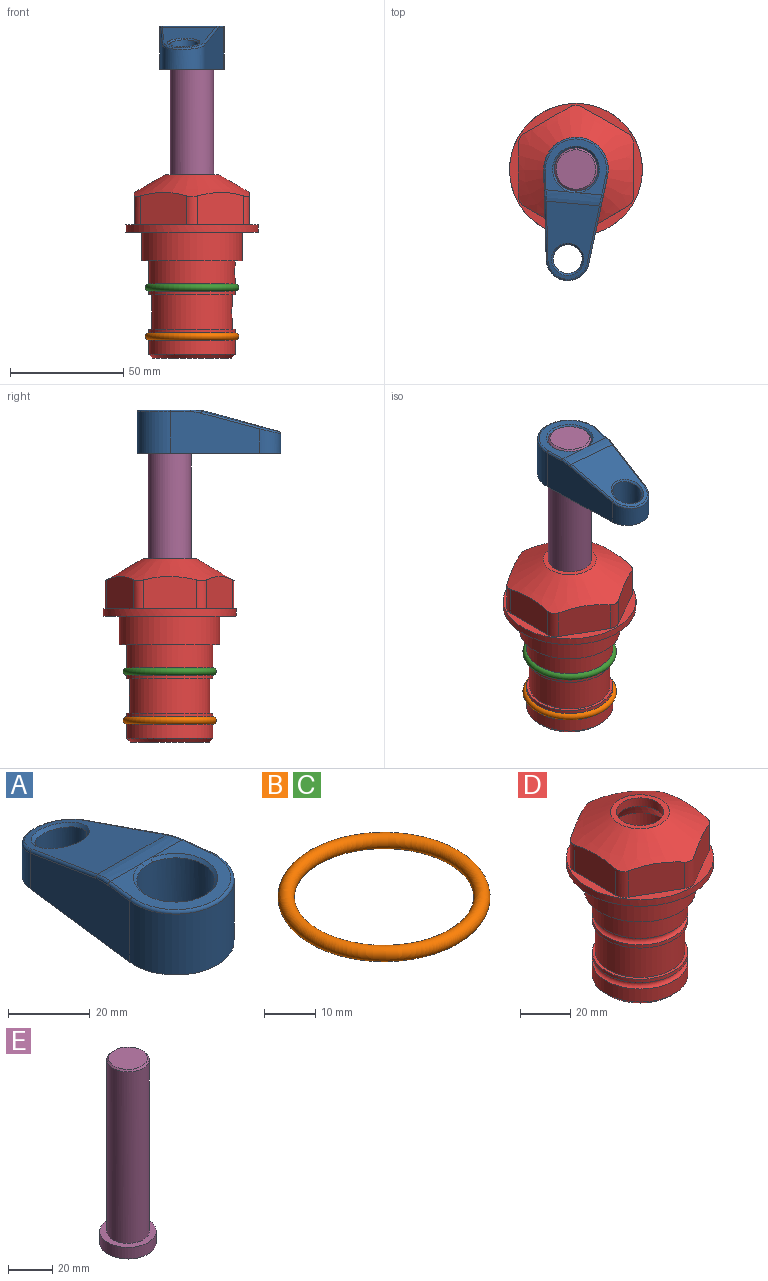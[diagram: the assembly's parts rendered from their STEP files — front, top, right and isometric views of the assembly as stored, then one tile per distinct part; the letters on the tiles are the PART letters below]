
ASSEMBLY  parts=5 mates=4
PART A: 31 faces, bbox 31.7x65.5x19.8 mm
  f0: plane 39.12x18.26mm, normal (0.99,0.12,0), area 612.2mm2, adj f1,f4,f7,f11,f13,f15
  f1: cylinder r=9.53mm len=18.91mm, axis (0,0,-1), area 296.1mm2, adj f0,f2,f7,f17
  f2: plane 39.12x18.26mm, normal (-0.99,0.12,0), area 612.2mm2, adj f1,f4,f7,f12,f14,f16
  f3: cylinder r=6.35mm len=12.7mm, axis (0,0,-1), area 362.4mm2, adj f7,f18
  f4: cylinder r=14.29mm len=28.58mm, axis (0,0,-1), area 882.2mm2, adj f0,f2,f7,f10
  f5: cylinder r=9.53mm len=19.05mm, axis (0,0,-1), area 1092.6mm2, adj f7,f19,f20
  f6: plane 26.99x23.69mm, normal (0,0,1), area 216.2mm2, adj f9,f10,f11,f12,f19
  f7: plane 63.5x28.58mm, normal (0,0,-1), area 661.8mm2, adj f0,f1,f2,f3,f4,f5,f22,f23
  f8: plane 33.52x23.6mm, normal (0,0.26,0.97), area 486mm2, adj f9,f15,f16,f17,f18
  f9: cylinder r=19.05mm len=24.72mm, axis (1,0,0), area 120.4mm2, adj f6,f8,f13,f14,f20
  f10: torus R=13.49mm, axis (0,0,1), area 59mm2, adj f4,f6,f11,f12
  f11: cylinder r=0.79mm len=8.67mm, axis (0.12,-0.99,0), area 10.8mm2, adj f0,f6,f10,f13
  f12: cylinder r=0.79mm len=8.67mm, axis (0.12,0.99,0), area 10.8mm2, adj f2,f6,f10,f14
  f13: bspline ~4.95x1.42mm, area 6.1mm2, adj f0,f9,f11,f15
  f14: bspline ~4.95x1.42mm, area 6.1mm2, adj f2,f9,f12,f16
  f15: cylinder r=0.79mm len=25.95mm, axis (0.12,-0.96,0.26), area 32.9mm2, adj f0,f8,f13,f17
  f16: cylinder r=0.79mm len=25.95mm, axis (0.12,0.96,-0.26), area 32.9mm2, adj f2,f8,f14,f17
  f17: bspline ~18.91x8.38mm, area 30mm2, adj f1,f8,f15,f16
  f18: bspline ~14.29x14.29mm, area 48.3mm2, adj f3,f8
  f19: cone r=9.53mm half-angle=45deg, axis (0,0,1), area 66.5mm2, adj f5,f6,f20
  f20: bspline ~3.22x0.96mm, area 3.5mm2, adj f5,f9,f19
  f21: plane 2.75x2.72mm, normal (0,0,-1), area 2.9mm2, adj f23,f25,f28
  f22: plane 23.05x15.88mm, normal (-0.99,-0.12,0), area 323.6mm2, adj f7,f25,f26,f27,f28,f29
  f23: plane 23.05x15.88mm, normal (0.99,-0.12,0), area 323.6mm2, adj f7,f21,f25,f27,f28,f30
  f24: cylinder r=9.53mm len=10.69mm, axis (0,0,-1), area 114.7mm2, adj f7,f27,f29,f30
  f25: cylinder r=12.7mm len=20.59mm, axis (0,0,-1), area 381.1mm2, adj f7,f21,f22,f23,f26,f28
  f26: plane 2.75x2.72mm, normal (0,0,-1), area 2.9mm2, adj f22,f25,f28
  f27: plane 19.72x18.37mm, normal (0,-0.26,-0.97), area 291.8mm2, adj f22,f23,f24,f28,f29,f30
  f28: cylinder r=15.88mm len=19.92mm, axis (1,0,0), area 54.8mm2, adj f21,f22,f23,f25,f26,f27
  f29: cylinder r=1.59mm len=11mm, axis (0,0,-1), area 34.7mm2, adj f7,f22,f24,f27
  f30: cylinder r=1.59mm len=11mm, axis (0,0,-1), area 34.7mm2, adj f7,f23,f24,f27
PART B: 1 faces, bbox 44.7x44.7x3.2 mm
  f0: torus R=19.05mm, axis (0,0,1), area 1193.9mm2
PART C: same geometry as B
PART D: 36 faces, bbox 58.7x58.7x81 mm
  f0: cylinder r=17.78mm len=35.56mm, axis (0,0,1), area 1670.8mm2, adj f23,f24,f31
  f1: cylinder r=19.05mm len=38.1mm, axis (0,0,1), area 1191.9mm2, adj f26,f27,f30
  f2: plane 58.66x58.66mm, normal (0,0,-1), area 1150.6mm2, adj f3,f28
  f3: cylinder r=29.33mm len=58.66mm, axis (0,0,-1), area 585.1mm2, adj f2,f4
  f4: plane 58.66x58.66mm, normal (0,0,1), area 475.9mm2, adj f3,f5,f6,f7,f8,f9,f10,f11
  f5: plane 20.32x14.34mm, normal (-0.5,0.87,0), area 324.4mm2, adj f4,f15,f16,f17
  f6: plane 20.32x14.34mm, normal (0.5,0.87,0), area 324.4mm2, adj f4,f14,f15,f17
  f7: plane 23.48x14.34mm, normal (1,0,0), area 324.4mm2, adj f4,f13,f14,f17
  f8: plane 20.32x14.34mm, normal (0.5,-0.87,0), area 324.4mm2, adj f4,f12,f13,f17
  f9: plane 20.32x14.34mm, normal (-0.5,-0.87,0), area 324.4mm2, adj f4,f11,f12,f17
  f10: plane 23.48x14.34mm, normal (-1,0,0), area 324.4mm2, adj f4,f11,f16,f17
  f11: cylinder r=5.08mm len=12.85mm, axis (0,0,-1), area 67.2mm2, adj f4,f9,f10,f17
  f12: cylinder r=5.08mm len=12.85mm, axis (0,0,-1), area 67.2mm2, adj f4,f8,f9,f17
  f13: cylinder r=5.08mm len=12.85mm, axis (0,0,-1), area 67.2mm2, adj f4,f7,f8,f17
  f14: cylinder r=5.08mm len=12.85mm, axis (0,0,-1), area 67.2mm2, adj f4,f6,f7,f17
  f15: cylinder r=5.08mm len=12.85mm, axis (0,0,-1), area 67.2mm2, adj f4,f5,f6,f17
  f16: cylinder r=5.08mm len=12.85mm, axis (0,0,-1), area 67.2mm2, adj f4,f5,f10,f17
  f17: cone r=11.73mm half-angle=60deg, axis (0,0,-1), area 2071.8mm2, adj f5,f6,f7,f8,f9,f10,f11,f12
  f18: plane 23.46x23.46mm, normal (0,0,1), area 147.4mm2, adj f17,f35
  f19: plane 34.93x34.93mm, normal (0,0,-1), area 958mm2, adj f29
  f20: cylinder r=19.05mm len=38.1mm, axis (0,0,1), area 760.1mm2, adj f21,f29
  f21: torus R=19.05mm, axis (0,0,1), area 565.3mm2, adj f20,f22
  f22: cylinder r=19.05mm len=38.1mm, axis (0,0,1), area 190mm2, adj f21,f23
  f23: plane 38.1x38.1mm, normal (0,0,1), area 146.9mm2, adj f0,f22
  f24: plane 38.1x38.1mm, normal (0,0,-1), area 146.9mm2, adj f0,f25
  f25: cylinder r=19.05mm len=38.1mm, axis (0,0,1), area 190mm2, adj f24,f26
  f26: torus R=19.05mm, axis (0,0,1), area 565.3mm2, adj f1,f25
  f27: plane 44.45x44.45mm, normal (0,0,-1), area 411.7mm2, adj f1,f28
  f28: cylinder r=22.23mm len=44.45mm, axis (0,0,1), area 1773.5mm2, adj f2,f27
  f29: cone r=19.05mm half-angle=45deg, axis (0,0,1), area 257.5mm2, adj f19,f20
  f30: cylinder r=3.17mm len=6.75mm, axis (-1,0,0), area 128mm2, adj f1,f33
  f31: cylinder r=3.17mm len=6.35mm, axis (-1,0,0), area 102.5mm2, adj f0,f33
  f32: plane 25.4x25.4mm, normal (0,0,1), area 506.7mm2, adj f33
  f33: cylinder r=12.7mm len=66.42mm, axis (0,0,-1), area 5236.2mm2, adj f30,f31,f32,f34
  f34: cone r=9.53mm half-angle=30deg, axis (0,0,-1), area 443.4mm2, adj f33,f35
  f35: cylinder r=9.53mm len=19.05mm, axis (0,0,-1), area 240.9mm2, adj f18,f34
PART E: 6 faces, bbox 25.4x25.4x101.6 mm
  f0: plane 17.46x17.46mm, normal (0,0,1), area 239.5mm2, adj f5
  f1: plane 25.4x25.4mm, normal (0,0,-1), area 506.7mm2, adj f2
  f2: cylinder r=12.7mm len=25.4mm, axis (0,0,1), area 506.7mm2, adj f1,f3
  f3: plane 25.4x25.4mm, normal (0,0,1), area 221.7mm2, adj f2,f4
  f4: cylinder r=9.53mm len=94.46mm, axis (0,0,1), area 5653mm2, adj f3,f5
  f5: cone r=8.73mm half-angle=45deg, axis (0,0,-1), area 64.4mm2, adj f0,f4
PLACE A rot(axis=(0,0,1),174.8deg) t=(0,0,27.55)mm
PLACE B t=(0,0,-21.59)mm
PLACE C at identity
PLACE D at identity fixed
PLACE E rot(axis=(0,0,1),174.8deg) t=(0,0,27.55)mm
MATE fastened C.f0 <-> D.f0  axis (0,0,1) through (0,0,-24.51)mm
MATE fastened B.f0 <-> D.f0  axis (0,0,1) through (0,0,-46.1)mm
MATE cylindrical E.f2 <-> D.f0  axis (0,0,-1) through (0,0,-10.55)mm
MATE fastened A.f4 <-> E.f2  axis (0,0,1) through (0,0,91.05)mm
